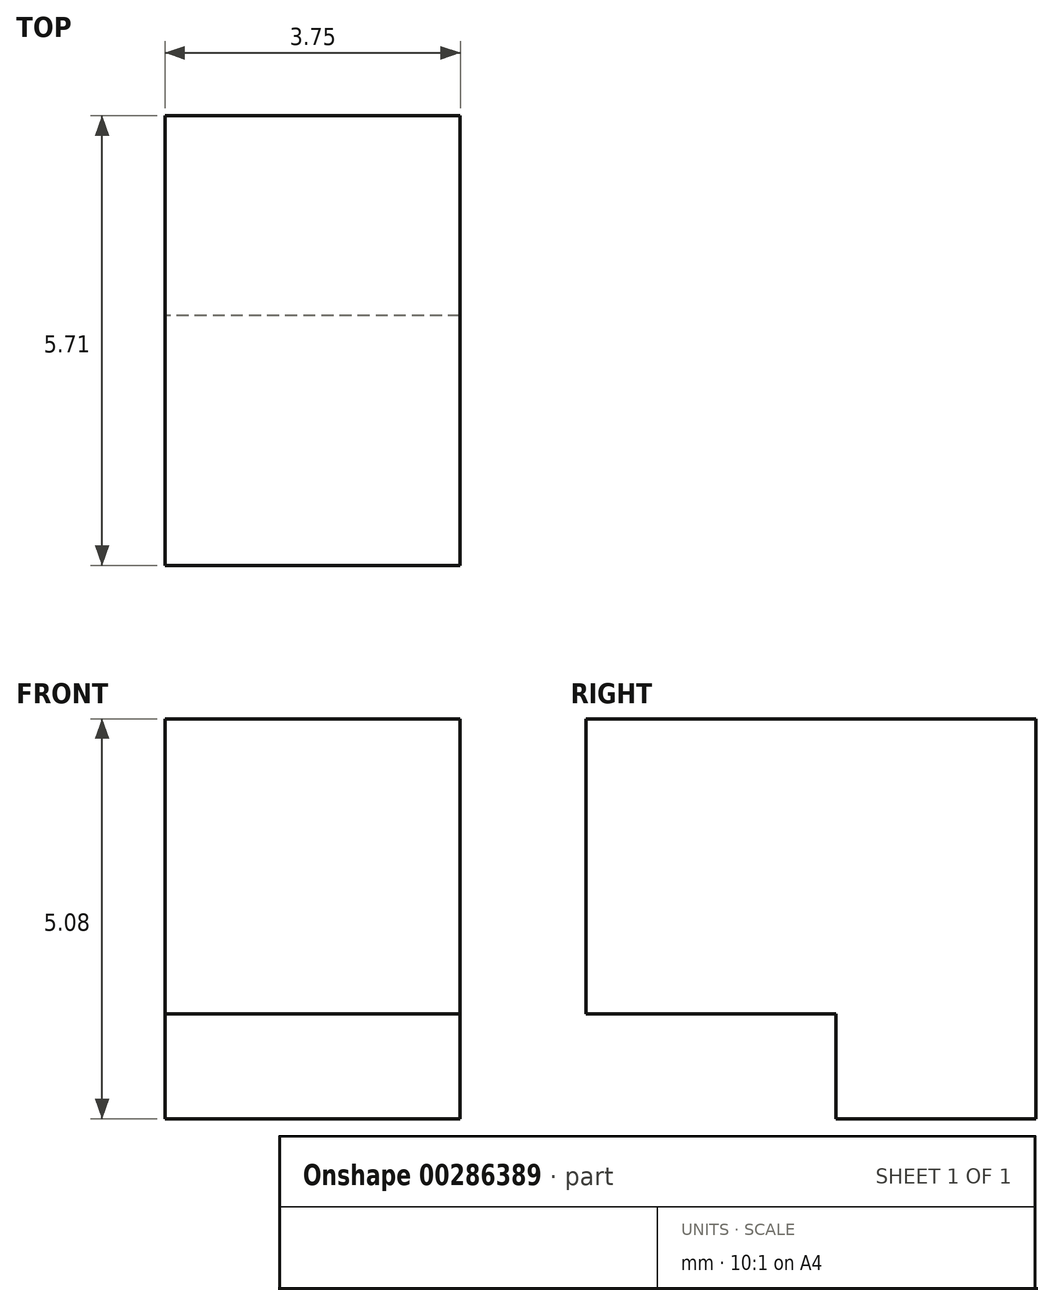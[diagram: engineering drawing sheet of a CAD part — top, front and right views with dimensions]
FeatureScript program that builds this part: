
annotation { "Feature Type Name" : "Feature", "Feature Type Description" : "" }
export const myFeature = defineFeature(function(context is Context, id is Id, definition is map)
    precondition{}
    {
        {
            var Q0;
            Q0=qCreatedBy(makeId("Right.planeOp"),FACE);
            var sketch = newSketch(context, id + "F0", { "sketchPlane" : qUnion([Q0])});
            skLineSegment(sketch, "E0", {"start": v(0, 0) * mm, "end": v(2.54, 0) * mm});
            skLineSegment(sketch, "E1", {"start": v(2.54, 0) * mm, "end": v(2.54, 5.08) * mm});
            skLineSegment(sketch, "E2", {"start": v(2.54, 5.08) * mm, "end": v(-3.18, 5.08) * mm});
            skLineSegment(sketch, "E3", {"start": v(-3.18, 5.08) * mm, "end": v(-3.18, 1.33) * mm});
            skLineSegment(sketch, "E4", {"start": v(-3.18, 1.33) * mm, "end": v(0, 1.33) * mm});
            skLineSegment(sketch, "E5", {"start": v(0, 1.33) * mm, "end": v(0, 0) * mm});
            skSolve(sketch);
        }
        {
            var Q0;
            Q0 = qSketchRegion(id + "F0", true);
            extrude(context, id + "F1", {"entities" : qUnion([Q0]), "depth" : 3.75 * mm});
        }
    });
